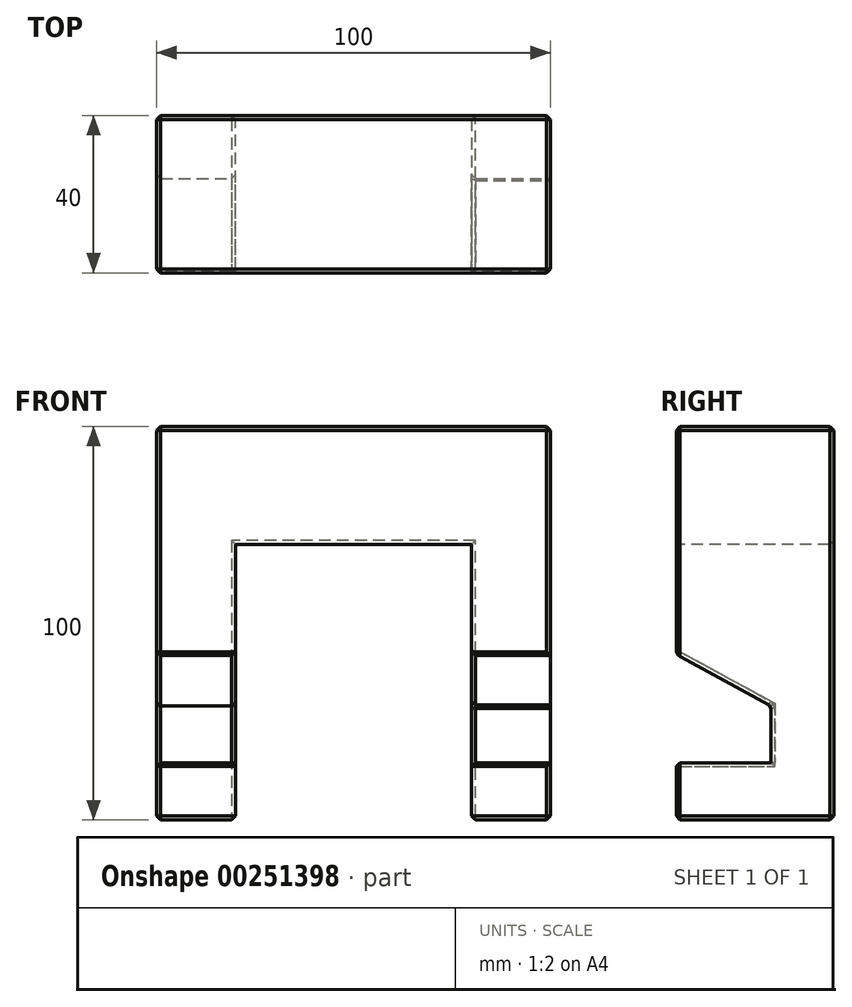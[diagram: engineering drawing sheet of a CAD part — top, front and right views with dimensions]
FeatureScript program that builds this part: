
annotation { "Feature Type Name" : "Feature", "Feature Type Description" : "" }
export const myFeature = defineFeature(function(context is Context, id is Id, definition is map)
    precondition{}
    {
        {
            var Q0;
            Q0=qCreatedBy(makeId("Front.planeOp"),FACE);
            var sketch = newSketch(context, id + "F0", { "sketchPlane" : qUnion([Q0])});
            skLineSegment(sketch, "E0.bottom", {"start": v(-50.63, 71) * mm, "end": v(49.37, 71) * mm});
            skLineSegment(sketch, "E0.top", {"start": v(-50.63, -29) * mm, "end": v(49.37, -29) * mm});
            skLineSegment(sketch, "E0.left", {"start": v(-50.63, 71) * mm, "end": v(-50.63, -29) * mm});
            skLineSegment(sketch, "E0.right", {"start": v(49.37, 71) * mm, "end": v(49.37, -29) * mm});
            skSolve(sketch);
        }
        {
            var Q0;
            Q0 = qSketchRegion(id + "F0", true);
            extrude(context, id + "F1", {"entities" : qUnion([Q0]), "depth" : 40 * mm});
        }
        {
            var Q0;
            Q0=makeQuery(id+"F1.opExtrude","CAP_FACE",FACE,{"disambiguationData":[OSD([sQuery(id+"F0.wireOp",EDGE,"E0.bottom"),sQuery(id+"F0.wireOp",EDGE,"E0.top"),sQuery(id+"F0.wireOp",EDGE,"E0.left"),sQuery(id+"F0.wireOp",EDGE,"E0.right")])],"isStart":false});
            var sketch = newSketch(context, id + "F2", { "sketchPlane" : qUnion([Q0])});
            skLineSegment(sketch, "E1.0", {"start": v(-50.63, 71) * mm, "end": v(49.37, 71) * mm});
            skLineSegment(sketch, "E1.1", {"start": v(49.37, 71) * mm, "end": v(49.37, -29) * mm});
            skLineSegment(sketch, "E1.2", {"start": v(-50.63, -29) * mm, "end": v(49.37, -29) * mm});
            skLineSegment(sketch, "E2.0.0", {"start": v(-50.63, 71) * mm, "end": v(-50.63, -29) * mm, "construction": true});
            skLineSegment(sketch, "E2.0.1", {"start": v(-50.63, -29) * mm, "end": v(49.37, -29) * mm, "construction": true});
            skLineSegment(sketch, "E2.0.2", {"start": v(49.37, -29) * mm, "end": v(49.37, 71) * mm, "construction": true});
            skLineSegment(sketch, "E2.0.3", {"start": v(49.37, 71) * mm, "end": v(-50.63, 71) * mm, "construction": true});
            skLineSegment(sketch, "E3.bottom", {"start": v(-30.63, 41) * mm, "end": v(29.37, 41) * mm});
            skLineSegment(sketch, "E3.top", {"start": v(-30.63, -47.9) * mm, "end": v(29.37, -47.9) * mm});
            skLineSegment(sketch, "E3.left", {"start": v(-30.63, 41) * mm, "end": v(-30.63, -47.9) * mm});
            skLineSegment(sketch, "E3.right", {"start": v(29.37, 41) * mm, "end": v(29.37, -47.9) * mm});
            skSolve(sketch);
        }
        {
            var Q0;
            Q0 = qSketchRegion(id + "F2", true);
            extrude(context, id + "F3", {"entities" : qUnion([Q0]), "operationType" : NewBodyOperationType.REMOVE, "oppositeDirection" : true, "depth" : 90.2 * mm});
        }
        {
            var Q0;
            Q0=makeQuery(id+"F1.opExtrude","SWEPT_FACE",FACE,{"disambiguationData":[OSD([sQuery(id+"F0.wireOp",EDGE,"E0.right")])]});
            var sketch = newSketch(context, id + "F4", { "sketchPlane" : qUnion([Q0])});
            skLineSegment(sketch, "E4", {"start": v(-47.72, 17.32) * mm, "end": v(-15.97, 0) * mm});
            skLineSegment(sketch, "E5", {"start": v(-15.97, 0) * mm, "end": v(-15.97, -14.43) * mm});
            skLineSegment(sketch, "E6", {"start": v(-15.97, -14.43) * mm, "end": v(-47.9, -14.43) * mm});
            skLineSegment(sketch, "E7", {"start": v(-47.9, -14.43) * mm, "end": v(-47.72, 17.32) * mm});
            skSolve(sketch);
        }
        {
            var Q0;
            Q0 = qSketchRegion(id + "F4", true);
            extrude(context, id + "F5", {"entities" : qUnion([Q0]), "operationType" : NewBodyOperationType.REMOVE, "oppositeDirection" : true, "depth" : 123.9 * mm});
        }
        {
            var Q0;
            {var subQ0=sQuery(id+"F0.wireOp",EDGE,"E0.bottom");var subQ1=sQuery(id+"F0.wireOp",EDGE,"E0.left");Q0=makeQuery(id+"F5.boolean.opBoolean","SPLIT",EDGE,{"disambiguationData":[TD([makeQuery(id+"F1.opExtrude","SWEPT_FACE",FACE,{"disambiguationData":[OSD([subQ0])]})])],"derivedFrom":makeQuery(id+"F1.opExtrude","CAP_EDGE",EDGE,{"disambiguationData":[OSD([subQ1])],"isStart":false})});}
            var Q1;
            Q1=makeQuery(id+"F1.opExtrude","CAP_EDGE",EDGE,{"disambiguationData":[OSD([sQuery(id+"F0.wireOp",EDGE,"E0.bottom")])],"isStart":false});
            var Q2;
            {var subQ0=sQuery(id+"F0.wireOp",EDGE,"E0.bottom");var subQ1=sQuery(id+"F0.wireOp",EDGE,"E0.right");Q2=makeQuery(id+"F5.boolean.opBoolean","SPLIT",EDGE,{"disambiguationData":[TD([makeQuery(id+"F1.opExtrude","SWEPT_FACE",FACE,{"disambiguationData":[OSD([subQ0])]})])],"derivedFrom":makeQuery(id+"F1.opExtrude","CAP_EDGE",EDGE,{"disambiguationData":[OSD([subQ1])],"isStart":false})});}
            var Q3;
            Q3=makeQuery(id+"F3.boolean.opBoolean","COPY",EDGE,{"derivedFrom":makeQuery(id+"F3.opExtrude","CAP_EDGE",EDGE,{"disambiguationData":[OSD([sQuery(id+"F2.wireOp",EDGE,"E3.bottom")])],"isStart":true})});
            var Q4;
            {var subQ0=sQuery(id+"F2.wireOp",EDGE,"E3.right");Q4=makeQuery(id+"F5.boolean.opBoolean","SPLIT",EDGE,{"disambiguationData":[TD([makeQuery(id+"F3.boolean.opBoolean","COPY",FACE,{"derivedFrom":makeQuery(id+"F3.opExtrude","SWEPT_FACE",FACE,{"disambiguationData":[OSD([sQuery(id+"F2.wireOp",EDGE,"E3.bottom")])]})})])],"derivedFrom":makeQuery(id+"F3.boolean.opBoolean","COPY",EDGE,{"derivedFrom":makeQuery(id+"F3.opExtrude","CAP_EDGE",EDGE,{"disambiguationData":[OSD([subQ0])],"isStart":true})})});}
            var Q5;
            Q5=makeQuery(id+"F5.boolean.opBoolean","INTERSECT",EDGE,{"disambiguationData":[OD(0.0)],"derivedFrom":[makeQuery(id+"F1.opExtrude","CAP_FACE",FACE,{"disambiguationData":[OSD([sQuery(id+"F0.wireOp",EDGE,"E0.bottom"),sQuery(id+"F0.wireOp",EDGE,"E0.top"),sQuery(id+"F0.wireOp",EDGE,"E0.left"),sQuery(id+"F0.wireOp",EDGE,"E0.right")])],"isStart":false}),makeQuery(id+"F5.opExtrude","SWEPT_FACE",FACE,{"disambiguationData":[OSD([sQuery(id+"F4.wireOp",EDGE,"E4")])]})]});
            var Q6;
            Q6=makeQuery(id+"F5.boolean.opBoolean","INTERSECT",EDGE,{"derivedFrom":[makeQuery(id+"F3.boolean.opBoolean","COPY",FACE,{"derivedFrom":makeQuery(id+"F3.opExtrude","SWEPT_FACE",FACE,{"disambiguationData":[OSD([sQuery(id+"F2.wireOp",EDGE,"E3.right")])]})}),makeQuery(id+"F5.opExtrude","SWEPT_FACE",FACE,{"disambiguationData":[OSD([sQuery(id+"F4.wireOp",EDGE,"E4")])]})]});
            var Q7;
            Q7=makeQuery(id+"F5.boolean.opBoolean","COPY",EDGE,{"derivedFrom":makeQuery(id+"F5.opExtrude","CAP_EDGE",EDGE,{"disambiguationData":[OSD([sQuery(id+"F4.wireOp",EDGE,"E4")])],"isStart":true})});
            var Q8;
            {var subQ0=sQuery(id+"F4.wireOp",EDGE,"E4");var subQ1=sQuery(id+"F4.wireOp",EDGE,"E5");Q8=makeQuery(id+"F5.boolean.opBoolean","COPY",EDGE,{"disambiguationData":[TD([makeQuery(id+"F1.opExtrude","SWEPT_FACE",FACE,{"disambiguationData":[OSD([sQuery(id+"F0.wireOp",EDGE,"E0.right")])]})])],"derivedFrom":makeQuery(id+"F5.opExtrude","SWEPT_EDGE",EDGE,{"disambiguationData":[OSD([subQ0,subQ1])]})});}
            var Q9;
            Q9=makeQuery(id+"F5.boolean.opBoolean","COPY",EDGE,{"derivedFrom":makeQuery(id+"F5.opExtrude","CAP_EDGE",EDGE,{"disambiguationData":[OSD([sQuery(id+"F4.wireOp",EDGE,"E5")])],"isStart":true})});
            var Q10;
            Q10=makeQuery(id+"F5.boolean.opBoolean","INTERSECT",EDGE,{"derivedFrom":[makeQuery(id+"F3.boolean.opBoolean","COPY",FACE,{"derivedFrom":makeQuery(id+"F3.opExtrude","SWEPT_FACE",FACE,{"disambiguationData":[OSD([sQuery(id+"F2.wireOp",EDGE,"E3.right")])]})}),makeQuery(id+"F5.opExtrude","SWEPT_FACE",FACE,{"disambiguationData":[OSD([sQuery(id+"F4.wireOp",EDGE,"E6")])]})]});
            var Q11;
            {var subQ0=sQuery(id+"F0.wireOp",EDGE,"E0.top");var subQ1=sQuery(id+"F2.wireOp",EDGE,"E3.right");Q11=makeQuery(id+"F5.boolean.opBoolean","SPLIT",EDGE,{"disambiguationData":[TD([makeQuery(id+"F1.opExtrude","SWEPT_FACE",FACE,{"disambiguationData":[OSD([subQ0])]})])],"derivedFrom":makeQuery(id+"F3.boolean.opBoolean","COPY",EDGE,{"derivedFrom":makeQuery(id+"F3.opExtrude","CAP_EDGE",EDGE,{"disambiguationData":[OSD([subQ1])],"isStart":true})})});}
            var Q12;
            {var subQ0=sQuery(id+"F0.wireOp",EDGE,"E0.right");var subQ1=sQuery(id+"F0.wireOp",EDGE,"E0.top");Q12=makeQuery(id+"F5.boolean.opBoolean","SPLIT",EDGE,{"disambiguationData":[TD([makeQuery(id+"F1.opExtrude","SWEPT_FACE",FACE,{"disambiguationData":[OSD([subQ1])]})])],"derivedFrom":makeQuery(id+"F1.opExtrude","CAP_EDGE",EDGE,{"disambiguationData":[OSD([subQ0])],"isStart":false})});}
            var Q13;
            Q13=makeQuery(id+"F3.boolean.opBoolean","INTERSECT",EDGE,{"derivedFrom":[makeQuery(id+"F1.opExtrude","SWEPT_FACE",FACE,{"disambiguationData":[OSD([sQuery(id+"F0.wireOp",EDGE,"E0.top")])]}),makeQuery(id+"F3.opExtrude","SWEPT_FACE",FACE,{"disambiguationData":[OSD([sQuery(id+"F2.wireOp",EDGE,"E3.right")])]})]});
            var Q14;
            {var subQ0=sQuery(id+"F0.wireOp",EDGE,"E0.right");var subQ1=sQuery(id+"F0.wireOp",EDGE,"E0.top");Q14=makeQuery(id+"F3.boolean.opBoolean","SPLIT",EDGE,{"disambiguationData":[TD([makeQuery(id+"F1.opExtrude","SWEPT_FACE",FACE,{"disambiguationData":[OSD([subQ0])]})])],"derivedFrom":makeQuery(id+"F1.opExtrude","CAP_EDGE",EDGE,{"disambiguationData":[OSD([subQ1])],"isStart":false})});}
            var Q15;
            Q15=makeQuery(id+"F1.opExtrude","SWEPT_EDGE",EDGE,{"disambiguationData":[OSD([sQuery(id+"F0.wireOp",EDGE,"E0.top"),sQuery(id+"F0.wireOp",EDGE,"E0.right")])]});
            var Q16;
            {var subQ0=sQuery(id+"F0.wireOp",EDGE,"E0.left");var subQ1=sQuery(id+"F0.wireOp",EDGE,"E0.top");Q16=makeQuery(id+"F3.boolean.opBoolean","SPLIT",EDGE,{"disambiguationData":[TD([makeQuery(id+"F1.opExtrude","SWEPT_FACE",FACE,{"disambiguationData":[OSD([subQ0])]})])],"derivedFrom":makeQuery(id+"F1.opExtrude","CAP_EDGE",EDGE,{"disambiguationData":[OSD([subQ1])],"isStart":false})});}
            var Q17;
            Q17=makeQuery(id+"F5.boolean.opBoolean","INTERSECT",EDGE,{"disambiguationData":[OD(1.0)],"derivedFrom":[makeQuery(id+"F1.opExtrude","CAP_FACE",FACE,{"disambiguationData":[OSD([sQuery(id+"F0.wireOp",EDGE,"E0.bottom"),sQuery(id+"F0.wireOp",EDGE,"E0.top"),sQuery(id+"F0.wireOp",EDGE,"E0.left"),sQuery(id+"F0.wireOp",EDGE,"E0.right")])],"isStart":false}),makeQuery(id+"F5.opExtrude","SWEPT_FACE",FACE,{"disambiguationData":[OSD([sQuery(id+"F4.wireOp",EDGE,"E6")])]})]});
            var Q18;
            {var subQ0=sQuery(id+"F0.wireOp",EDGE,"E0.left");var subQ1=sQuery(id+"F0.wireOp",EDGE,"E0.top");Q18=makeQuery(id+"F5.boolean.opBoolean","SPLIT",EDGE,{"disambiguationData":[TD([makeQuery(id+"F1.opExtrude","SWEPT_FACE",FACE,{"disambiguationData":[OSD([subQ1])]})])],"derivedFrom":makeQuery(id+"F1.opExtrude","CAP_EDGE",EDGE,{"disambiguationData":[OSD([subQ0])],"isStart":false})});}
            var Q19;
            {var subQ0=sQuery(id+"F0.wireOp",EDGE,"E0.top");var subQ1=sQuery(id+"F2.wireOp",EDGE,"E3.left");Q19=makeQuery(id+"F5.boolean.opBoolean","SPLIT",EDGE,{"disambiguationData":[TD([makeQuery(id+"F1.opExtrude","SWEPT_FACE",FACE,{"disambiguationData":[OSD([subQ0])]})])],"derivedFrom":makeQuery(id+"F3.boolean.opBoolean","COPY",EDGE,{"derivedFrom":makeQuery(id+"F3.opExtrude","CAP_EDGE",EDGE,{"disambiguationData":[OSD([subQ1])],"isStart":true})})});}
            var Q20;
            Q20=makeQuery(id+"F5.boolean.opBoolean","INTERSECT",EDGE,{"derivedFrom":[makeQuery(id+"F1.opExtrude","SWEPT_FACE",FACE,{"disambiguationData":[OSD([sQuery(id+"F0.wireOp",EDGE,"E0.left")])]}),makeQuery(id+"F5.opExtrude","SWEPT_FACE",FACE,{"disambiguationData":[OSD([sQuery(id+"F4.wireOp",EDGE,"E6")])]})]});
            var Q21;
            Q21=makeQuery(id+"F5.boolean.opBoolean","INTERSECT",EDGE,{"derivedFrom":[makeQuery(id+"F3.boolean.opBoolean","COPY",FACE,{"derivedFrom":makeQuery(id+"F3.opExtrude","SWEPT_FACE",FACE,{"disambiguationData":[OSD([sQuery(id+"F2.wireOp",EDGE,"E3.left")])]})}),makeQuery(id+"F5.opExtrude","SWEPT_FACE",FACE,{"disambiguationData":[OSD([sQuery(id+"F4.wireOp",EDGE,"E4")])]})]});
            var Q22;
            {var subQ0=sQuery(id+"F2.wireOp",EDGE,"E3.left");Q22=makeQuery(id+"F5.boolean.opBoolean","SPLIT",EDGE,{"disambiguationData":[TD([makeQuery(id+"F3.boolean.opBoolean","COPY",FACE,{"derivedFrom":makeQuery(id+"F3.opExtrude","SWEPT_FACE",FACE,{"disambiguationData":[OSD([sQuery(id+"F2.wireOp",EDGE,"E3.bottom")])]})})])],"derivedFrom":makeQuery(id+"F3.boolean.opBoolean","COPY",EDGE,{"derivedFrom":makeQuery(id+"F3.opExtrude","CAP_EDGE",EDGE,{"disambiguationData":[OSD([subQ0])],"isStart":true})})});}
            var Q23;
            Q23=makeQuery(id+"F5.boolean.opBoolean","INTERSECT",EDGE,{"derivedFrom":[makeQuery(id+"F1.opExtrude","SWEPT_FACE",FACE,{"disambiguationData":[OSD([sQuery(id+"F0.wireOp",EDGE,"E0.left")])]}),makeQuery(id+"F5.opExtrude","SWEPT_FACE",FACE,{"disambiguationData":[OSD([sQuery(id+"F4.wireOp",EDGE,"E5")])]})]});
            var Q24;
            Q24=makeQuery(id+"F5.boolean.opBoolean","INTERSECT",EDGE,{"derivedFrom":[makeQuery(id+"F3.boolean.opBoolean","COPY",FACE,{"derivedFrom":makeQuery(id+"F3.opExtrude","SWEPT_FACE",FACE,{"disambiguationData":[OSD([sQuery(id+"F2.wireOp",EDGE,"E3.left")])]})}),makeQuery(id+"F5.opExtrude","SWEPT_FACE",FACE,{"disambiguationData":[OSD([sQuery(id+"F4.wireOp",EDGE,"E5")])]})]});
            var Q25;
            Q25=makeQuery(id+"F1.opExtrude","SWEPT_EDGE",EDGE,{"disambiguationData":[OSD([sQuery(id+"F0.wireOp",EDGE,"E0.top"),sQuery(id+"F0.wireOp",EDGE,"E0.left")])]});
            var Q26;
            Q26=makeQuery(id+"F3.boolean.opBoolean","INTERSECT",EDGE,{"derivedFrom":[makeQuery(id+"F1.opExtrude","SWEPT_FACE",FACE,{"disambiguationData":[OSD([sQuery(id+"F0.wireOp",EDGE,"E0.top")])]}),makeQuery(id+"F3.opExtrude","SWEPT_FACE",FACE,{"disambiguationData":[OSD([sQuery(id+"F2.wireOp",EDGE,"E3.left")])]})]});
            var Q27;
            Q27=makeQuery(id+"F3.boolean.opBoolean","INTERSECT",EDGE,{"derivedFrom":[makeQuery(id+"F1.opExtrude","CAP_FACE",FACE,{"disambiguationData":[OSD([sQuery(id+"F0.wireOp",EDGE,"E0.bottom"),sQuery(id+"F0.wireOp",EDGE,"E0.top"),sQuery(id+"F0.wireOp",EDGE,"E0.left"),sQuery(id+"F0.wireOp",EDGE,"E0.right")])],"isStart":true}),makeQuery(id+"F3.opExtrude","SWEPT_FACE",FACE,{"disambiguationData":[OSD([sQuery(id+"F2.wireOp",EDGE,"E3.bottom")])]})]});
            var Q28;
            Q28=makeQuery(id+"F3.boolean.opBoolean","INTERSECT",EDGE,{"derivedFrom":[makeQuery(id+"F1.opExtrude","CAP_FACE",FACE,{"disambiguationData":[OSD([sQuery(id+"F0.wireOp",EDGE,"E0.bottom"),sQuery(id+"F0.wireOp",EDGE,"E0.top"),sQuery(id+"F0.wireOp",EDGE,"E0.left"),sQuery(id+"F0.wireOp",EDGE,"E0.right")])],"isStart":true}),makeQuery(id+"F3.opExtrude","SWEPT_FACE",FACE,{"disambiguationData":[OSD([sQuery(id+"F2.wireOp",EDGE,"E3.right")])]})]});
            var Q29;
            {var subQ0=sQuery(id+"F0.wireOp",EDGE,"E0.right");var subQ1=sQuery(id+"F0.wireOp",EDGE,"E0.top");Q29=makeQuery(id+"F3.boolean.opBoolean","SPLIT",EDGE,{"disambiguationData":[TD([makeQuery(id+"F1.opExtrude","SWEPT_FACE",FACE,{"disambiguationData":[OSD([subQ0])]})])],"derivedFrom":makeQuery(id+"F1.opExtrude","CAP_EDGE",EDGE,{"disambiguationData":[OSD([subQ1])],"isStart":true})});}
            var Q30;
            {var subQ0=sQuery(id+"F0.wireOp",EDGE,"E0.left");var subQ1=sQuery(id+"F0.wireOp",EDGE,"E0.top");Q30=makeQuery(id+"F3.boolean.opBoolean","SPLIT",EDGE,{"disambiguationData":[TD([makeQuery(id+"F1.opExtrude","SWEPT_FACE",FACE,{"disambiguationData":[OSD([subQ0])]})])],"derivedFrom":makeQuery(id+"F1.opExtrude","CAP_EDGE",EDGE,{"disambiguationData":[OSD([subQ1])],"isStart":true})});}
            var Q31;
            Q31=makeQuery(id+"F1.opExtrude","CAP_EDGE",EDGE,{"disambiguationData":[OSD([sQuery(id+"F0.wireOp",EDGE,"E0.left")])],"isStart":true});
            var Q32;
            Q32=makeQuery(id+"F5.boolean.opBoolean","INTERSECT",EDGE,{"derivedFrom":[makeQuery(id+"F1.opExtrude","SWEPT_FACE",FACE,{"disambiguationData":[OSD([sQuery(id+"F0.wireOp",EDGE,"E0.left")])]}),makeQuery(id+"F5.opExtrude","SWEPT_FACE",FACE,{"disambiguationData":[OSD([sQuery(id+"F4.wireOp",EDGE,"E4")])]})]});
            var Q33;
            Q33=makeQuery(id+"F1.opExtrude","CAP_EDGE",EDGE,{"disambiguationData":[OSD([sQuery(id+"F0.wireOp",EDGE,"E0.right")])],"isStart":true});
            var Q34;
            Q34=makeQuery(id+"F1.opExtrude","SWEPT_EDGE",EDGE,{"disambiguationData":[OSD([sQuery(id+"F0.wireOp",EDGE,"E0.bottom"),sQuery(id+"F0.wireOp",EDGE,"E0.right")])]});
            var Q35;
            Q35=makeQuery(id+"F1.opExtrude","CAP_EDGE",EDGE,{"disambiguationData":[OSD([sQuery(id+"F0.wireOp",EDGE,"E0.bottom")])],"isStart":true});
            var Q36;
            Q36=makeQuery(id+"F1.opExtrude","SWEPT_EDGE",EDGE,{"disambiguationData":[OSD([sQuery(id+"F0.wireOp",EDGE,"E0.bottom"),sQuery(id+"F0.wireOp",EDGE,"E0.left")])]});
            var Q37;
            Q37=makeQuery(id+"F3.boolean.opBoolean","INTERSECT",EDGE,{"derivedFrom":[makeQuery(id+"F1.opExtrude","CAP_FACE",FACE,{"disambiguationData":[OSD([sQuery(id+"F0.wireOp",EDGE,"E0.bottom"),sQuery(id+"F0.wireOp",EDGE,"E0.top"),sQuery(id+"F0.wireOp",EDGE,"E0.left"),sQuery(id+"F0.wireOp",EDGE,"E0.right")])],"isStart":true}),makeQuery(id+"F3.opExtrude","SWEPT_FACE",FACE,{"disambiguationData":[OSD([sQuery(id+"F2.wireOp",EDGE,"E3.left")])]})]});
            chamfer(context, id + "F6", {"entities" : qUnion([Q0, Q1, Q2, Q3, Q4, Q5, Q6, Q7, Q8, Q9, Q10, Q11, Q12, Q13, Q14, Q15, Q16, Q17, Q18, Q19, Q20, Q21, Q22, Q23, Q24, Q25, Q26, Q27, Q28, Q29, Q30, Q31, Q32, Q33, Q34, Q35, Q36, Q37]), "width" : 1 * mm, "tangentPropagation" : true});
        }
    });
